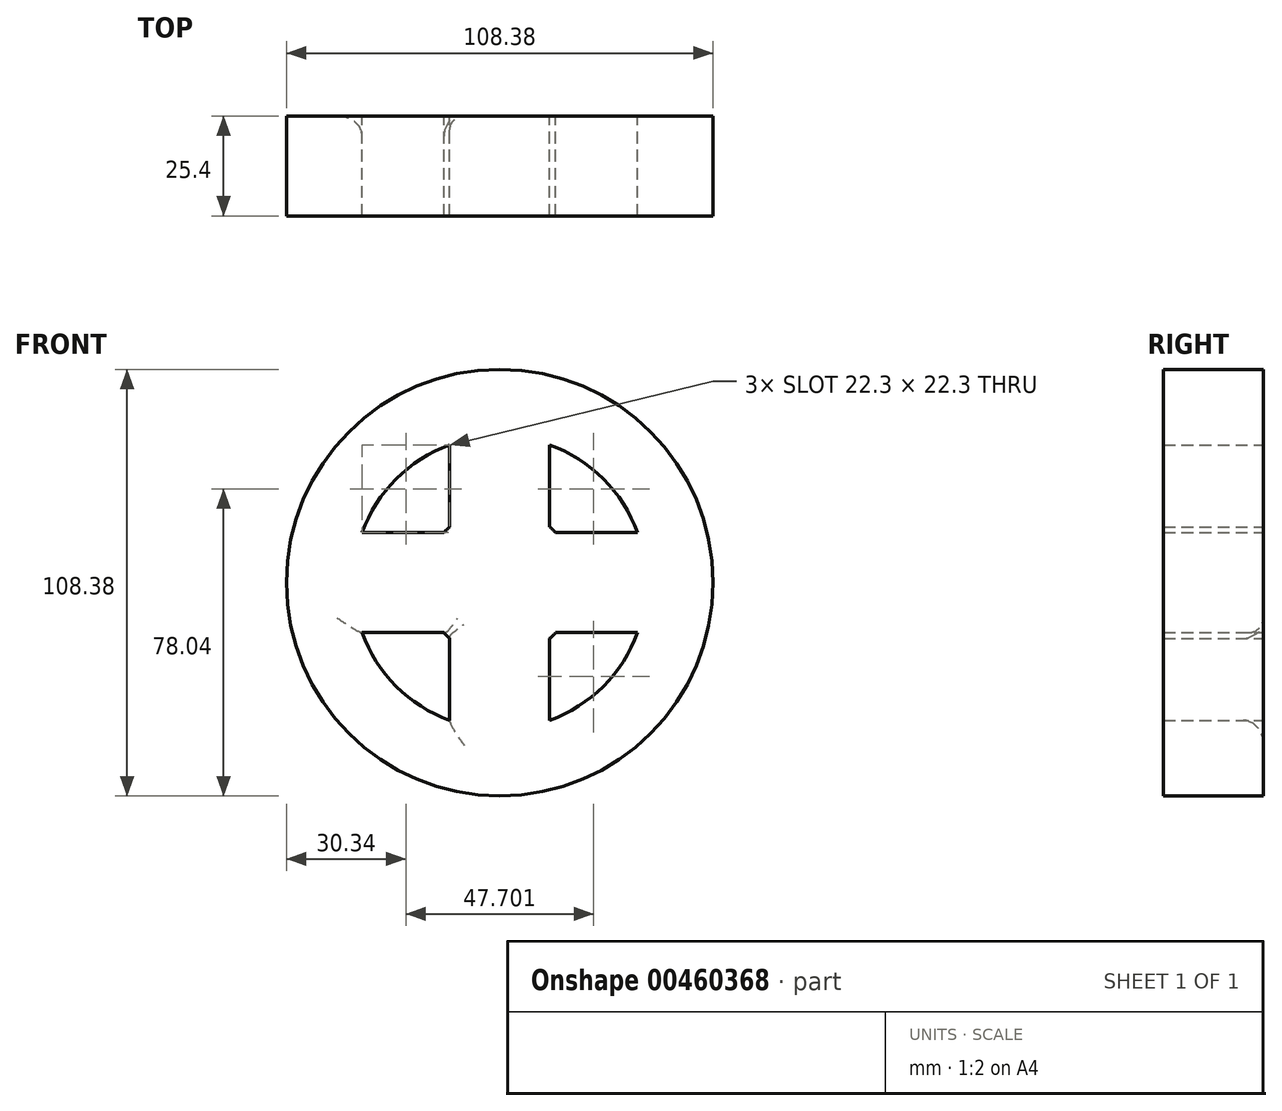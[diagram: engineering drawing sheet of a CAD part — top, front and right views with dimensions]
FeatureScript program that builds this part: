
annotation { "Feature Type Name" : "Feature", "Feature Type Description" : "" }
export const myFeature = defineFeature(function(context is Context, id is Id, definition is map)
    precondition{}
    {
        {
            var Q0;
            Q0=qCreatedBy(makeId("Front.planeOp"),FACE);
            var sketch = newSketch(context, id + "F0", { "sketchPlane" : qUnion([Q0])});
            skCircle(sketch, "E0", {"center": v(0, 0) * mm, "radius": 54.2 * mm});
            skArc(sketch, "E1", {"start": v(-35, -12.7) * mm, "mid": v(37.23, 0) * mm, "end": v(-35, 12.7) * mm});
            skArc(sketch, "E2", {"start": v(-14.2, -12.7) * mm, "mid": v(-13.47, -13.47) * mm, "end": v(-12.7, -14.2) * mm});
            skLineSegment(sketch, "E3", {"start": v(0, 0) * mm, "end": v(0, 37.23) * mm, "construction": true});
            skLineSegment(sketch, "E4", {"start": v(0, 0) * mm, "end": v(37.23, 0) * mm, "construction": true});
            skLineSegment(sketch, "E5", {"start": v(0, 0) * mm, "end": v(0, -37.23) * mm, "construction": true});
            skLineSegment(sketch, "E6", {"start": v(0, 0) * mm, "end": v(-37.23, 0) * mm, "construction": true});
            skLineSegment(sketch, "E7.0", {"start": v(12.7, 14.2) * mm, "end": v(12.7, 35) * mm});
            skLineSegment(sketch, "E8.0", {"start": v(-12.7, 14.2) * mm, "end": v(-12.7, 35) * mm});
            skLineSegment(sketch, "E9.0", {"start": v(14.2, -12.7) * mm, "end": v(35, -12.7) * mm});
            skLineSegment(sketch, "E10.0", {"start": v(14.2, 12.7) * mm, "end": v(35, 12.7) * mm});
            skLineSegment(sketch, "E11.0", {"start": v(-14.2, 12.7) * mm, "end": v(-35, 12.7) * mm});
            skLineSegment(sketch, "E12.0", {"start": v(-14.2, -12.7) * mm, "end": v(-35, -12.7) * mm});
            skLineSegment(sketch, "E13.0", {"start": v(-12.7, -14.2) * mm, "end": v(-12.7, -35) * mm});
            skLineSegment(sketch, "E14.0", {"start": v(12.7, -14.2) * mm, "end": v(12.7, -35) * mm});
            skArc(sketch, "E15.trimOffspring", {"start": v(-12.7, 14.2) * mm, "mid": v(-13.47, 13.47) * mm, "end": v(-14.2, 12.7) * mm});
            skArc(sketch, "E16.trimOffspring", {"start": v(12.7, -14.2) * mm, "mid": v(13.47, -13.47) * mm, "end": v(14.2, -12.7) * mm});
            skArc(sketch, "E17.trimOffspring", {"start": v(14.2, 12.7) * mm, "mid": v(13.47, 13.47) * mm, "end": v(12.7, 14.2) * mm});
            skSolve(sketch);
        }
        {
            var Q0;
            Q0=makeQuery(id+"F0.imprint","IMPRINT",FACE,{"disambiguationData":[TD([[makeQuery(id+"F0.imprint","IMPRINT",EDGE,{"derivedFrom":sQuery(id+"F0.wireOp",EDGE,"E0")}),1.0]])]});
            extrude(context, id + "F1", {"entities" : qUnion([Q0]), "depth" : 25.4 * mm});
        }
        {
            var Q0;
            {var subQ0=sQuery(id+"F0.wireOp",EDGE,"E1");Q0=makeQuery(id+"F1.opExtrude","CAP_EDGE",EDGE,{"disambiguationData":[OSD([subQ0]),TDD([makeQuery(id+"F0.imprint","IMPRINT",EDGE,{"disambiguationData":[TD([[makeQuery(id+"F0.imprint","INTERSECT",VERTEX,{"derivedFrom":[subQ0,sQuery(id+"F0.wireOp",EDGE,"E12.0")]}),-1.0]])],"derivedFrom":subQ0})])],"isStart":true});}
            fillet(context, id + "F2", {"entities" : qUnion([Q0]), "radius" : 5.08 * mm, "tangentPropagation" : true, "allowEdgeOverflow" : false});
        }
        {
            var Q0;
            Q0=makeQuery(id+"F1.opExtrude","CAP_EDGE",EDGE,{"disambiguationData":[OSD([sQuery(id+"F0.wireOp",EDGE,"E13.0")])],"isStart":true});
            fillet(context, id + "F3", {"entities" : qUnion([Q0]), "radius" : 3.66 * mm, "tangentPropagation" : true, "allowEdgeOverflow" : false});
        }
        {
            var Q0;
            Q0=makeQuery(id+"F1.opExtrude","CAP_EDGE",EDGE,{"disambiguationData":[OSD([sQuery(id+"F0.wireOp",EDGE,"E12.0")])],"isStart":true});
            fillet(context, id + "F4", {"entities" : qUnion([Q0]), "radius" : 3.75 * mm, "tangentPropagation" : true, "allowEdgeOverflow" : false});
        }
        {
            var Q0;
            Q0=makeQuery(id+"F1.opExtrude","CAP_EDGE",EDGE,{"disambiguationData":[OSD([sQuery(id+"F0.wireOp",EDGE,"E2")])],"isStart":true});
            fillet(context, id + "F5", {"entities" : qUnion([Q0]), "radius" : 5.08 * mm, "tangentPropagation" : true, "allowEdgeOverflow" : false});
        }
    });
